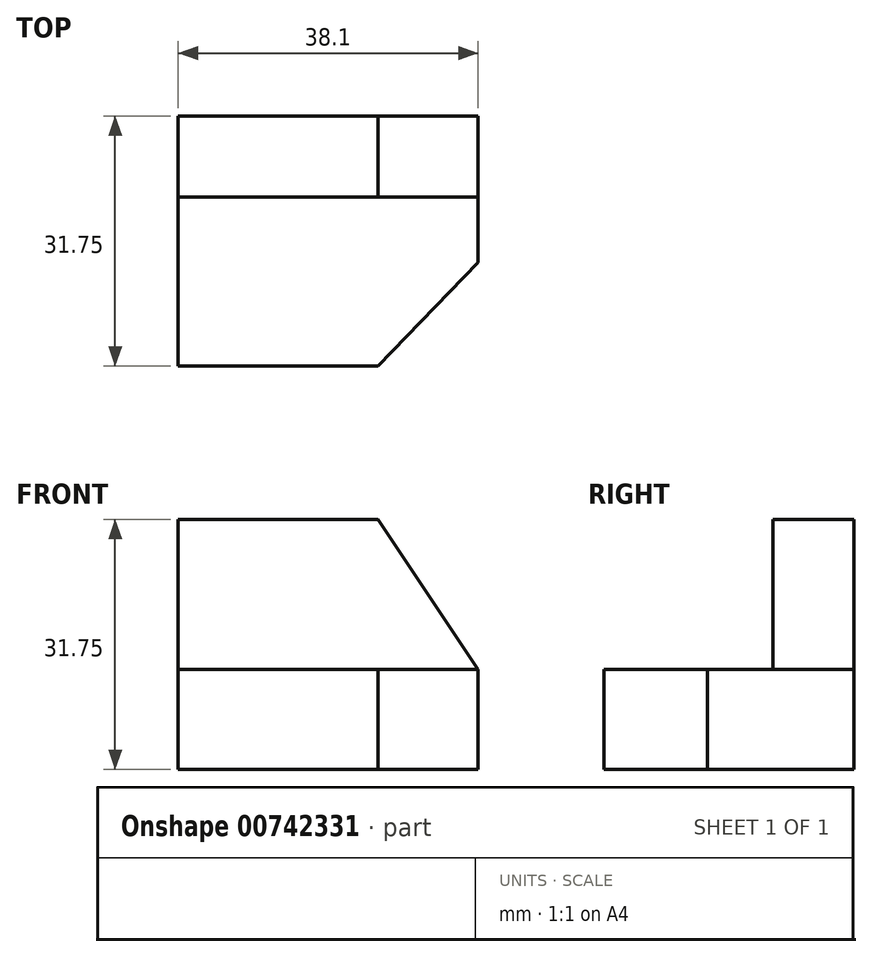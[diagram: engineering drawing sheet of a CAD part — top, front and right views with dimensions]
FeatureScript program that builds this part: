
annotation { "Feature Type Name" : "Feature", "Feature Type Description" : "" }
export const myFeature = defineFeature(function(context is Context, id is Id, definition is map)
    precondition{}
    {
        {
            var Q0;
            Q0=qCreatedBy(makeId("Right.planeOp"),FACE);
            var sketch = newSketch(context, id + "F0", { "sketchPlane" : qUnion([Q0])});
            skLineSegment(sketch, "E0", {"start": v(0, 0) * mm, "end": v(-31.75, 0) * mm});
            skLineSegment(sketch, "E1", {"start": v(-31.75, 0) * mm, "end": v(-31.75, 12.7) * mm});
            skLineSegment(sketch, "E2", {"start": v(-31.75, 12.7) * mm, "end": v(-10.3, 12.7) * mm});
            skLineSegment(sketch, "E3", {"start": v(-10.3, 12.7) * mm, "end": v(-10.3, 31.75) * mm});
            skLineSegment(sketch, "E4", {"start": v(-10.3, 31.75) * mm, "end": v(0, 31.75) * mm});
            skLineSegment(sketch, "E5", {"start": v(0, 31.75) * mm, "end": v(0, 0) * mm});
            skSolve(sketch);
        }
        {
            var Q0;
            Q0=qCreatedBy(makeId("Right.planeOp"),FACE);
            var sketch = newSketch(context, id + "F1", { "sketchPlane" : qUnion([Q0])});
            skSolve(sketch);
        }
        {
            var Q0;
            Q0 = qSketchRegion(id + "F1", true);
            var Q1;
            Q1=makeQuery(id+"F0.imprint","IMPRINT",FACE,{"disambiguationData":[TD([[makeQuery(id+"F0.imprint","IMPRINT",EDGE,{"derivedFrom":sQuery(id+"F0.wireOp",EDGE,"E0")}),-1.0]])]});
            extrude(context, id + "F2", {"entities" : qUnion([Q0, Q1]), "depth" : 38.1 * mm, "offsetDistance" : 25.4 * mm});
        }
        {
            var Q0;
            Q0=makeQuery(id+"F2.opExtrude","SWEPT_FACE",FACE,{"disambiguationData":[OSD([sQuery(id+"F0.wireOp",EDGE,"E3")])]});
            var sketch = newSketch(context, id + "F3", { "sketchPlane" : qUnion([Q0])});
            skLineSegment(sketch, "E6", {"start": v(25.4, 31.75) * mm, "end": v(38.1, 12.7) * mm});
            skSolve(sketch);
        }
        {
            var Q0;
            Q0 = qSketchRegion(id + "F3", true);
            var Q1;
            {var subQ0=sQuery(id+"F3.wireOp",EDGE,"E6");Q1=makeQuery(id+"F3.imprint","IMPRINT",FACE,{"disambiguationData":[TD([[makeQuery(id+"F3.imprint","IMPRINT",EDGE,{"derivedFrom":subQ0}),1.0]])]});}
            extrude(context, id + "F4", {"entities" : qUnion([Q0, Q1]), "operationType" : NewBodyOperationType.REMOVE, "endBound" : BoundingType.THROUGH_ALL, "oppositeDirection" : true, "depth" : 25.4 * mm, "offsetDistance" : 25.4 * mm});
        }
        {
            var Q0;
            Q0=makeQuery(id+"F2.opExtrude","SWEPT_FACE",FACE,{"disambiguationData":[OSD([sQuery(id+"F0.wireOp",EDGE,"E2")])]});
            var sketch = newSketch(context, id + "F5", { "sketchPlane" : qUnion([Q0])});
            skLineSegment(sketch, "E7", {"start": v(38.1, -18.6) * mm, "end": v(25.4, -31.75) * mm});
            skSolve(sketch);
        }
        {
            var Q0;
            Q0 = qSketchRegion(id + "F5", true);
            var Q1;
            {var subQ0=sQuery(id+"F5.wireOp",EDGE,"E7");Q1=makeQuery(id+"F5.imprint","IMPRINT",FACE,{"disambiguationData":[TD([[makeQuery(id+"F5.imprint","IMPRINT",EDGE,{"derivedFrom":subQ0}),1.0]])]});}
            extrude(context, id + "F6", {"entities" : qUnion([Q0, Q1]), "operationType" : NewBodyOperationType.REMOVE, "endBound" : BoundingType.THROUGH_ALL, "oppositeDirection" : true, "depth" : 25.4 * mm, "offsetDistance" : 25.4 * mm});
        }
    });
